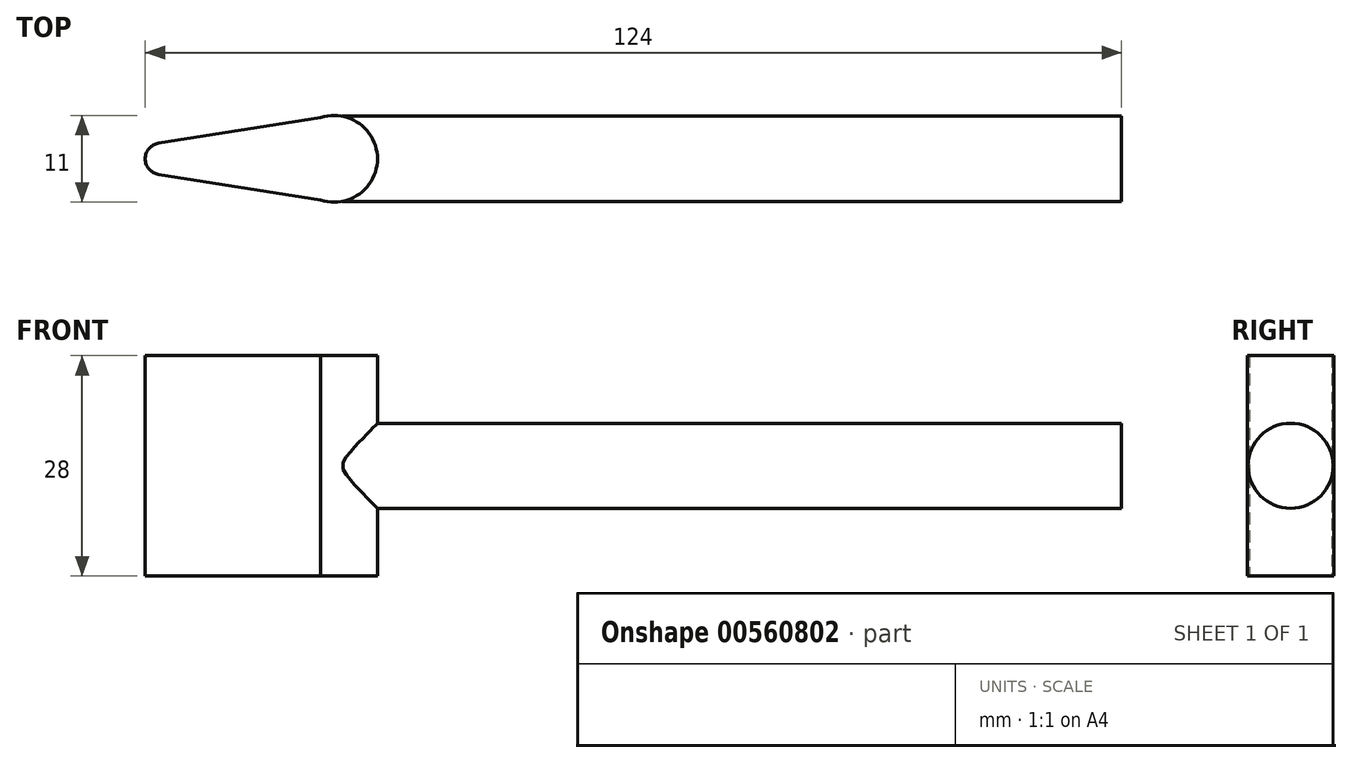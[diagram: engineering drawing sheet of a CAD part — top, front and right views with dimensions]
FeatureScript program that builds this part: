
annotation { "Feature Type Name" : "Feature", "Feature Type Description" : "" }
export const myFeature = defineFeature(function(context is Context, id is Id, definition is map)
    precondition{}
    {
        {
            var Q0;
            Q0=qCreatedBy(makeId("Top.planeOp"),FACE);
            var sketch = newSketch(context, id + "F0", { "sketchPlane" : qUnion([Q0])});
            skCircle(sketch, "E0", {"center": v(-22, 0) * mm, "radius": 2 * mm});
            skCircle(sketch, "E1", {"center": v(0, 0) * mm, "radius": 5.5 * mm});
            skLineSegment(sketch, "E2", {"start": v(-22, 0) * mm, "end": v(-122, 0) * mm, "construction": true});
            skLineSegment(sketch, "E3", {"start": v(0, 5.5) * mm, "end": v(-22.31, 1.98) * mm});
            skLineSegment(sketch, "E4", {"start": v(0, -5.5) * mm, "end": v(-22.31, -1.98) * mm});
            skSolve(sketch);
        }
        {
            var Q0;
            Q0 = qSketchRegion(id + "F0", true);
            extrude(context, id + "F1", {"entities" : qUnion([Q0]), "depth" : 14 * mm, "offsetDistance" : 25 * mm, "hasSecondDirection" : true, "secondDirectionOppositeDirection" : true, "secondDirectionDepth" : 14 * mm});
        }
        {
            var Q0;
            Q0=qCreatedBy(makeId("Right.planeOp"),FACE);
            var sketch = newSketch(context, id + "F2", { "sketchPlane" : qUnion([Q0])});
            skCircle(sketch, "E5", {"center": v(0, 0) * mm, "radius": 5.4 * mm});
            skSolve(sketch);
        }
        {
            var Q0;
            Q0 = qSketchRegion(id + "F2", true);
            extrude(context, id + "F3", {"entities" : qUnion([Q0]), "operationType" : NewBodyOperationType.ADD, "depth" : 100 * mm, "offsetDistance" : 25 * mm});
        }
    });
